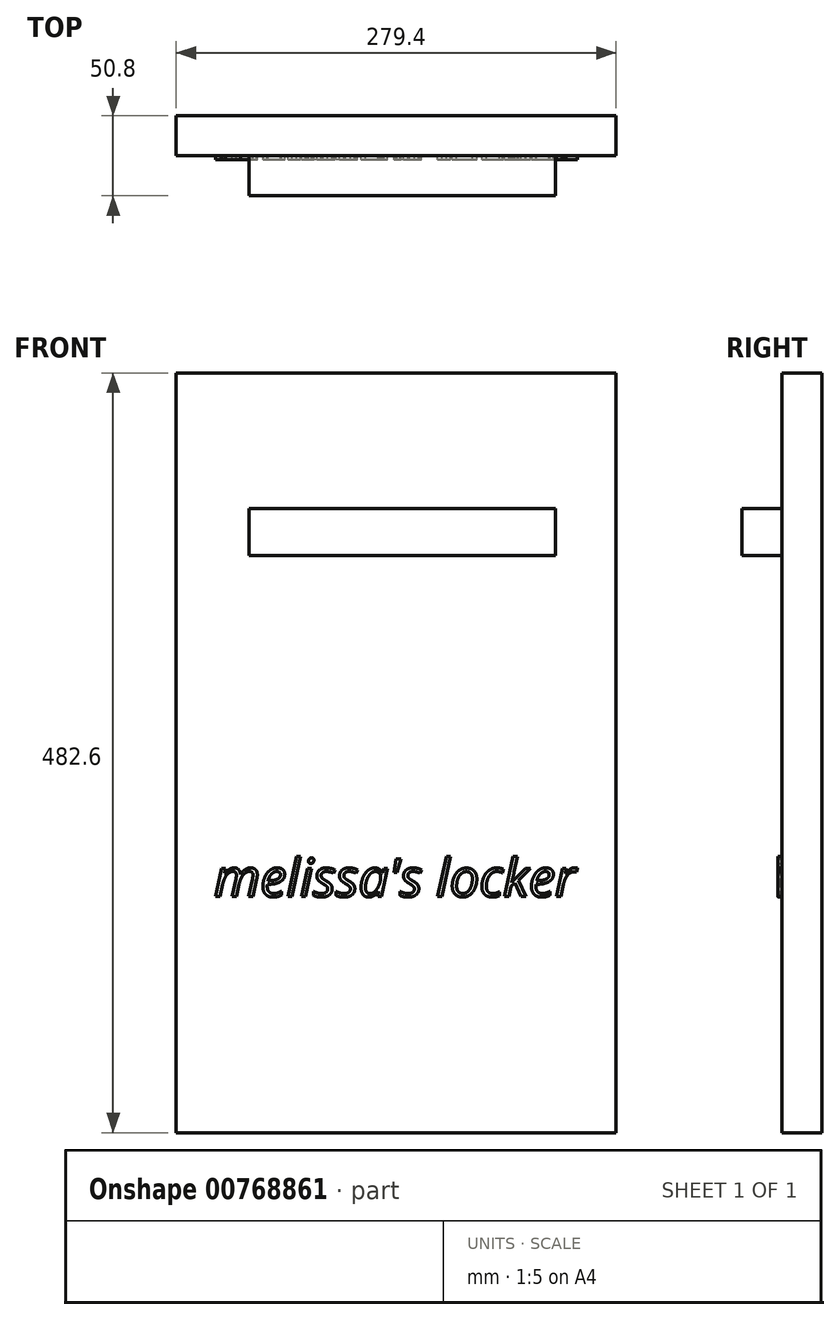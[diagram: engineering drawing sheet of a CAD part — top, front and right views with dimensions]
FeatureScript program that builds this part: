
annotation { "Feature Type Name" : "Feature", "Feature Type Description" : "" }
export const myFeature = defineFeature(function(context is Context, id is Id, definition is map)
    precondition{}
    {
        {
            var Q0;
            Q0=qCreatedBy(makeId("Front.planeOp"),FACE);
            var sketch = newSketch(context, id + "F0", { "sketchPlane" : qUnion([Q0])});
            skLineSegment(sketch, "E0.bottom", {"start": v(-144.28, 318.72) * mm, "end": v(135.12, 318.72) * mm});
            skLineSegment(sketch, "E0.top", {"start": v(-144.28, -163.88) * mm, "end": v(135.12, -163.88) * mm});
            skLineSegment(sketch, "E0.left", {"start": v(-144.28, 318.72) * mm, "end": v(-144.28, -163.88) * mm});
            skLineSegment(sketch, "E0.right", {"start": v(135.12, 318.72) * mm, "end": v(135.12, -163.88) * mm});
            skSolve(sketch);
        }
        {
            var Q0;
            Q0=makeQuery(id+"F0.imprint","IMPRINT",FACE,{"disambiguationData":[TD([[makeQuery(id+"F0.imprint","IMPRINT",EDGE,{"derivedFrom":sQuery(id+"F0.wireOp",EDGE,"E0.bottom")}),-1.0]])]});
            extrude(context, id + "F1", {"entities" : qUnion([Q0]), "depth" : 25.4 * mm, "offsetDistance" : 25.4 * mm});
        }
        {
            var Q0;
            Q0=makeQuery(id+"F1.opExtrude","CAP_FACE",FACE,{"disambiguationData":[OSD([sQuery(id+"F0.wireOp",EDGE,"E0.bottom"),sQuery(id+"F0.wireOp",EDGE,"E0.top"),sQuery(id+"F0.wireOp",EDGE,"E0.left"),sQuery(id+"F0.wireOp",EDGE,"E0.right")])],"isStart":false});
            var sketch = newSketch(context, id + "F2", { "sketchPlane" : qUnion([Q0])});
            skLineSegment(sketch, "E1.bottom", {"start": v(-97.9, 232.63) * mm, "end": v(96.48, 232.63) * mm});
            skLineSegment(sketch, "E1.top", {"start": v(-97.9, 202.65) * mm, "end": v(96.48, 202.65) * mm});
            skLineSegment(sketch, "E1.left", {"start": v(-97.9, 232.63) * mm, "end": v(-97.9, 202.65) * mm});
            skLineSegment(sketch, "E1.right", {"start": v(96.48, 232.63) * mm, "end": v(96.48, 202.65) * mm});
            skSolve(sketch);
        }
        {
            var Q0;
            Q0=makeQuery(id+"F2.imprint","IMPRINT",FACE,{"disambiguationData":[TD([[makeQuery(id+"F2.imprint","IMPRINT",EDGE,{"derivedFrom":sQuery(id+"F2.wireOp",EDGE,"E1.bottom")}),-1.0]])]});
            var sketch = newSketch(context, id + "F3", { "sketchPlane" : qUnion([Q0])});
            skSolve(sketch);
        }
        {
            var Q0;
            Q0=makeQuery(id+"F2.imprint","IMPRINT",FACE,{"disambiguationData":[TD([[makeQuery(id+"F2.imprint","IMPRINT",EDGE,{"derivedFrom":sQuery(id+"F2.wireOp",EDGE,"E1.bottom")}),1.0]])]});
            var sketch = newSketch(context, id + "F4", { "sketchPlane" : qUnion([Q0])});
            skText(sketch, "E2", { "text": "melissa\'s locker", "fontName": "OpenSans-Italic.ttf"});
            const initialGuessF4  = {"E2": [-0.12014, -0.01397, 1, 0, 0.02418]};
            skSetInitialGuess(sketch, initialGuessF4);
            skSolve(sketch);
        }
        {
            var Q0;
            Q0 = qSketchRegion(id + "F4", true);
            extrude(context, id + "F5", {"entities" : qUnion([Q0]), "operationType" : NewBodyOperationType.ADD, "depth" : 2.54 * mm, "offsetDistance" : 25.4 * mm});
        }
        {
            var Q0;
            Q0=makeQuery(id+"F3.imprint","IMPRINT",FACE,{"disambiguationData":[TD([[makeQuery(id+"F3.imprint","IMPRINT",EDGE,{"derivedFrom":makeQuery(id+"F2.imprint","IMPRINT",EDGE,{"derivedFrom":sQuery(id+"F2.wireOp",EDGE,"E1.bottom")})}),-1.0]])]});
            extrude(context, id + "F6", {"entities" : qUnion([Q0]), "operationType" : NewBodyOperationType.ADD, "depth" : 25.4 * mm, "offsetDistance" : 25.4 * mm});
        }
        {
            var Q0;
            Q0=makeQuery(id+"F2.imprint","IMPRINT",FACE,{"disambiguationData":[TD([[makeQuery(id+"F2.imprint","IMPRINT",EDGE,{"derivedFrom":sQuery(id+"F2.wireOp",EDGE,"E1.bottom")}),1.0]])]});
            var sketch = newSketch(context, id + "F7", { "sketchPlane" : qUnion([Q0])});
            skLineSegment(sketch, "E3.bottom", {"start": v(-84.24, 86.82) * mm, "end": v(92.4, 86.82) * mm});
            skLineSegment(sketch, "E3.top", {"start": v(-84.24, 26.01) * mm, "end": v(92.4, 26.01) * mm});
            skLineSegment(sketch, "E3.left", {"start": v(-84.24, 86.82) * mm, "end": v(-84.24, 26.01) * mm});
            skLineSegment(sketch, "E3.right", {"start": v(92.4, 86.82) * mm, "end": v(92.4, 26.01) * mm});
            skSolve(sketch);
        }
        {
            var Q0;
            Q0=sQuery(id+"F7.wireOp",EDGE,"E3.bottom");
            extrude(context, id + "F8", {"bodyType" : ToolBodyType.SURFACE, "surfaceEntities" : qUnion([Q0]), "depth" : 2.54 * mm, "offsetDistance" : 25.4 * mm});
        }
    });
